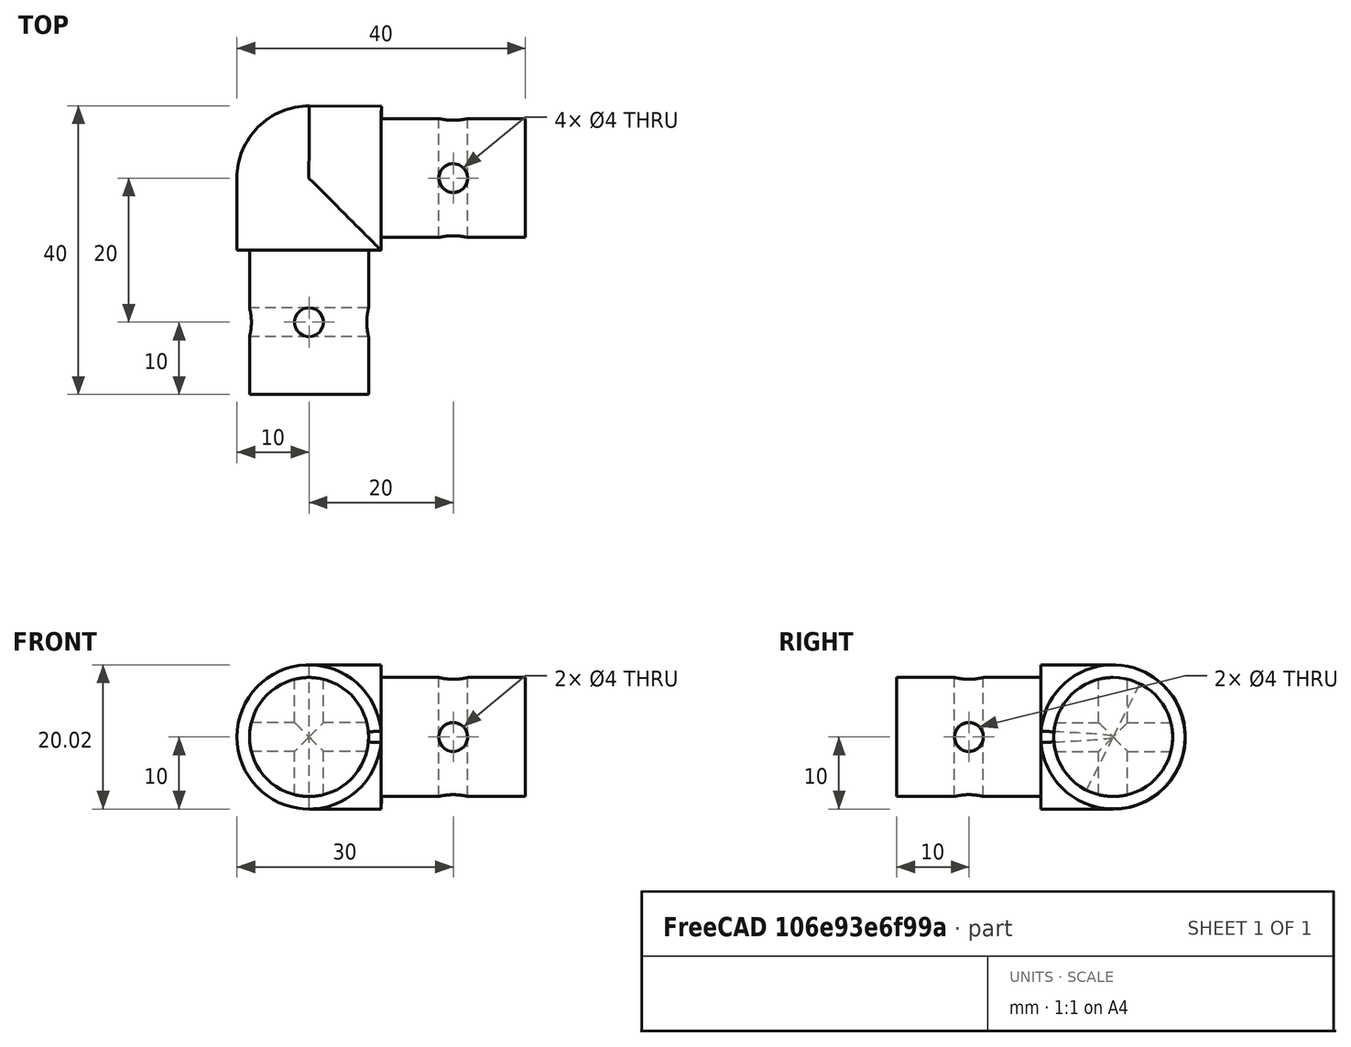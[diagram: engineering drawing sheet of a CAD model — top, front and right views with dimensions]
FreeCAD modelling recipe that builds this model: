
FCSTD DOCUMENT  (FreeCAD 0.18R16110 (Git))
Label: connector-l
License: All rights reserved
LicenseURL: http://en.wikipedia.org/wiki/All_rights_reserved
objects: Part::Cylinder×8, Part::MultiFuse×2, Part::Sphere×1, Part::Cut×1
note: 12 computed .brp shape members not serialized (recipe doc carries the construction recipe); baked Part::Feature solids carry a one-line shape summary decoded from their .brp

FEATURE [Part::Cylinder] Cylinder
  Angle = 360
  AttacherType = Attacher::AttachEngine3D
  Height = 20
  Placement = pos=(10,0,2.2e-15) rot=(0,1,0;1.5708rad)
  Radius = 8.25
FEATURE [Part::Cylinder] Cylinder001
  Angle = 360
  AttacherType = Attacher::AttachEngine3D
  Height = 20
  Placement = pos=(4e-15,-10,-2e-15) rot=(0.57735,0.57735,-0.57735;2.0944rad)
  Radius = 8.25
FEATURE [Part::Cylinder] Cylinder002
  Angle = 360
  AttacherType = Attacher::AttachEngine3D
  Height = 10
  Placement = pos=(0,2e-15,0) rot=(0.576173,-0.577056,0.578818;4.18702rad)
  Radius = 10
FEATURE [Part::Cylinder] Cylinder003
  Angle = 360
  AttacherType = Attacher::AttachEngine3D
  Height = 10
  Placement = pos=(0,0,2e-15) rot=(0,0.707107,-0.707107;3.14159rad)
  Radius = 10
FEATURE [Part::Sphere] Sphere
  Angle1 = -90
  Angle2 = 90
  Angle3 = 360
  AttacherType = Attacher::AttachEngine3D
  Radius = 10
FEATURE [Part::MultiFuse] Fusion  label="Positive Fusion"
  Shapes = -> [Cylinder,Sphere,Cylinder003,Cylinder002,Cylinder001]
FEATURE [Part::Cylinder] Cylinder004
  Angle = 360
  AttacherType = Attacher::AttachEngine3D
  Height = 20
  Placement = pos=(20,0,-10) rot=(0,0,1;0rad)
  Radius = 2
FEATURE [Part::Cylinder] Cylinder005
  Angle = 360
  AttacherType = Attacher::AttachEngine3D
  Height = 20
  Placement = pos=(0,-20,-10) rot=(0,0,1;0rad)
  Radius = 2
FEATURE [Part::Cylinder] Cylinder006
  Angle = 360
  AttacherType = Attacher::AttachEngine3D
  Height = 20
  Placement = pos=(20,-10,3e-15) rot=(0.57735,0.57735,0.57735;4.18879rad)
  Radius = 2
FEATURE [Part::Cylinder] Cylinder007
  Angle = 360
  AttacherType = Attacher::AttachEngine3D
  Height = 20
  Placement = pos=(10,-20,2e-15) rot=(0,-1,0;1.5708rad)
  Radius = 2
FEATURE [Part::MultiFuse] Fusion001  label="Negative Fusion"
  Shapes = -> [Cylinder004,Cylinder007,Cylinder005,Cylinder006]
FEATURE [Part::Cut] Cut
  Base = -> Fusion
  Tool = -> Fusion001
